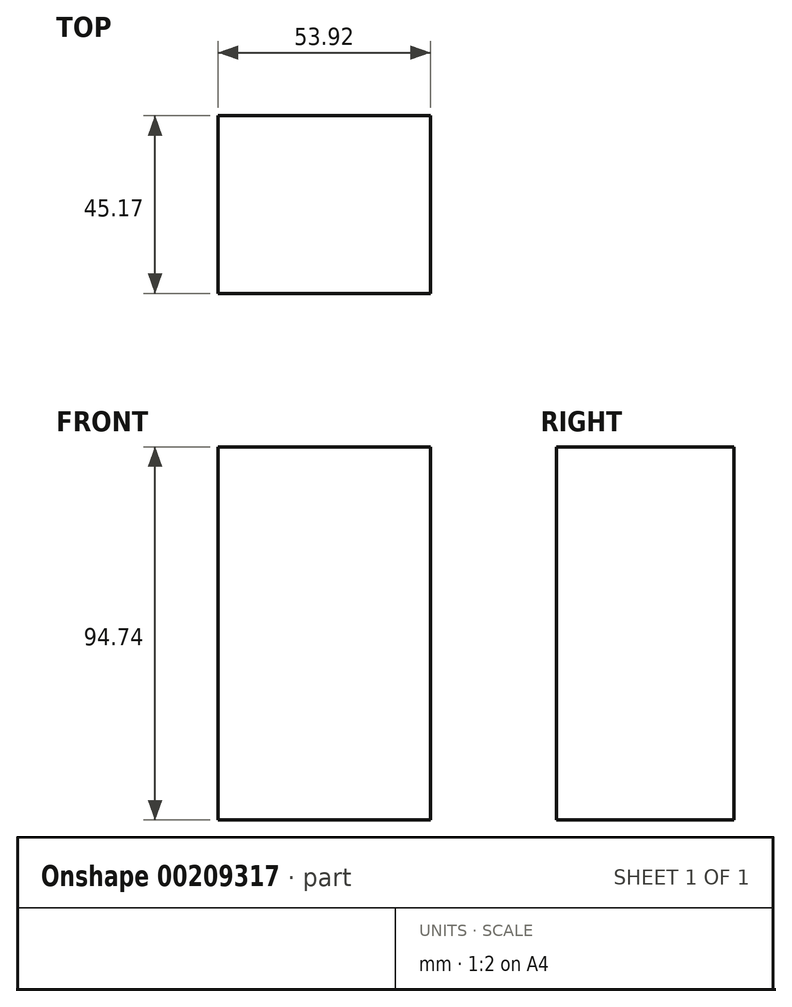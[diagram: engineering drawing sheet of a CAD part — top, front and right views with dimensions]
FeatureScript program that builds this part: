
annotation { "Feature Type Name" : "Feature", "Feature Type Description" : "" }
export const myFeature = defineFeature(function(context is Context, id is Id, definition is map)
    precondition{}
    {
        {
            var Q0;
            Q0=qCreatedBy(makeId("Top.planeOp"),FACE);
            var sketch = newSketch(context, id + "F0", { "sketchPlane" : qUnion([Q0])});
            skLineSegment(sketch, "E0.bottom", {"start": v(-25.94, 19.67) * mm, "end": v(27.98, 19.67) * mm});
            skLineSegment(sketch, "E0.top", {"start": v(-25.94, -25.5) * mm, "end": v(27.98, -25.5) * mm});
            skLineSegment(sketch, "E0.left", {"start": v(-25.94, 19.67) * mm, "end": v(-25.94, -25.5) * mm});
            skLineSegment(sketch, "E0.right", {"start": v(27.98, 19.67) * mm, "end": v(27.98, -25.5) * mm});
            skSolve(sketch);
        }
        {
            var Q0;
            Q0=makeQuery(id+"F0.imprint","IMPRINT",FACE,{"disambiguationData":[TD([[makeQuery(id+"F0.imprint","IMPRINT",EDGE,{"derivedFrom":sQuery(id+"F0.wireOp",EDGE,"E0.bottom")}),-1.0]])]});
            extrude(context, id + "F1", {"entities" : qUnion([Q0]), "depth" : 94.74 * mm});
        }
    });
